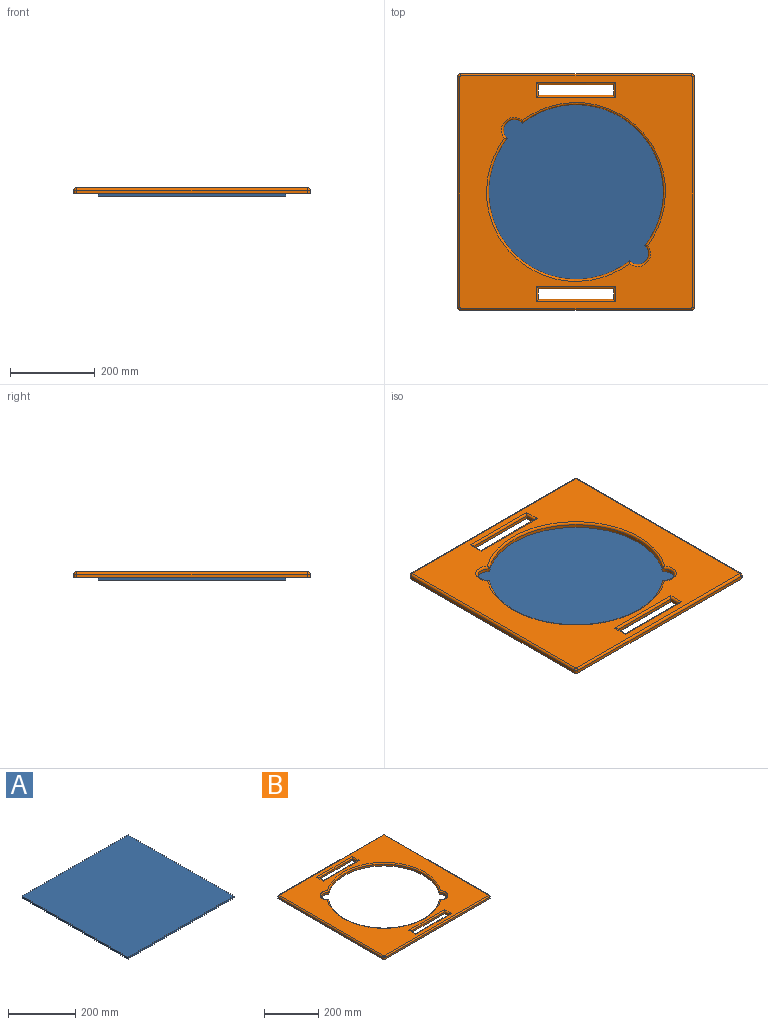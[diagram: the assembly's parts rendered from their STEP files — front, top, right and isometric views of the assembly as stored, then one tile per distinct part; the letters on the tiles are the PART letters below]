
ASSEMBLY  parts=2 mates=1
PART A: 6 faces, bbox 444.5x444.5x6.4 mm
  f0: plane 444.5x6.35mm, normal (0,-1,0), area 2822.6mm2, adj f1,f3,f4,f5
  f1: plane 444.5x6.35mm, normal (1,0,0), area 2822.6mm2, adj f0,f2,f4,f5
  f2: plane 444.5x6.35mm, normal (0,1,0), area 2822.6mm2, adj f1,f3,f4,f5
  f3: plane 444.5x6.35mm, normal (-1,0,0), area 2822.6mm2, adj f0,f2,f4,f5
  f4: plane 444.5x444.5mm, normal (0,0,1), area 197580.2mm2, adj f0,f1,f2,f3
  f5: plane 444.5x444.5mm, normal (0,0,-1), area 197580.2mm2, adj f0,f1,f2,f3
PART B: 42 faces, bbox 558.8x558.8x12.7 mm
  f0: plane 177.8x7.62mm, normal (0,-1,0), area 1354.8mm2, adj f1,f19,f21,f22
  f1: plane 25.4x7.62mm, normal (-1,0,0), area 193.5mm2, adj f0,f2,f21,f23
  f2: plane 177.8x7.62mm, normal (0,1,0), area 1354.8mm2, adj f1,f19,f21,f25
  f3: plane 546.1x7.62mm, normal (1,0,0), area 4161.3mm2, adj f4,f16,f21,f32
  f4: cylinder r=6.35mm len=7.62mm, axis (0,0,-1), area 76mm2, adj f3,f5,f21,f30
  f5: plane 546.1x7.62mm, normal (0,1,0), area 4161.3mm2, adj f4,f6,f21,f28
  f6: cylinder r=6.35mm len=7.62mm, axis (0,0,-1), area 76mm2, adj f5,f7,f21,f26
  f7: plane 546.1x7.62mm, normal (-1,0,0), area 4161.3mm2, adj f6,f8,f21,f27
  f8: cylinder r=6.35mm len=7.62mm, axis (0,0,-1), area 76mm2, adj f7,f9,f21,f29
  f9: plane 546.1x7.62mm, normal (0,-1,0), area 4161.3mm2, adj f8,f16,f21,f31
  f10: cylinder r=206.38mm len=333.27mm, axis (0,0,-1), area 4553.1mm2, adj f11,f17,f21,f35
  f11: cylinder r=25.4mm len=44.43mm, axis (0,0,-1), area 631.9mm2, adj f10,f12,f21,f34
  f12: cylinder r=206.38mm len=333.27mm, axis (0,0,-1), area 4553.1mm2, adj f11,f17,f21,f36
  f13: plane 25.4x7.62mm, normal (-1,0,0), area 193.5mm2, adj f14,f18,f21,f39
  f14: plane 177.8x7.62mm, normal (0,1,0), area 1354.8mm2, adj f13,f15,f21,f38
  f15: plane 25.4x7.62mm, normal (1,0,0), area 193.5mm2, adj f14,f18,f21,f40
  f16: cylinder r=6.35mm len=7.62mm, axis (0,0,-1), area 76mm2, adj f3,f9,f21,f33
  f17: cylinder r=25.4mm len=44.43mm, axis (0,0,-1), area 631.9mm2, adj f10,f12,f21,f37
  f18: plane 177.8x7.62mm, normal (0,-1,0), area 1354.8mm2, adj f13,f15,f21,f41
  f19: plane 25.4x7.62mm, normal (1,0,0), area 193.5mm2, adj f0,f2,f21,f24
  f20: plane 548.64x548.64mm, normal (0,0,1), area 144776.7mm2, adj f22,f23,f24,f25,f26,f27,f28,f29
  f21: plane 558.8x558.8mm, normal (0,0,-1), area 167308.4mm2, adj f0,f1,f2,f3,f4,f5,f6,f7
  f22: cylinder r=5.08mm len=187.96mm, axis (-1,0,0), area 1448.2mm2, adj f0,f20,f23,f24
  f23: cylinder r=5.08mm len=35.56mm, axis (0,1,0), area 232.1mm2, adj f1,f20,f22,f25
  f24: cylinder r=5.08mm len=35.56mm, axis (0,-1,0), area 232.1mm2, adj f19,f20,f22,f25
  f25: cylinder r=5.08mm len=187.96mm, axis (1,0,0), area 1448.2mm2, adj f2,f20,f23,f24
  f26: torus R=1.27mm, axis (0,0,1), area 56.5mm2, adj f6,f20,f27,f28
  f27: cylinder r=5.08mm len=546.1mm, axis (0,1,0), area 4357.7mm2, adj f7,f20,f26,f29
  f28: cylinder r=5.08mm len=546.1mm, axis (1,0,0), area 4357.7mm2, adj f5,f20,f26,f30
  f29: torus R=1.27mm, axis (0,0,1), area 56.5mm2, adj f8,f20,f27,f31
  f30: torus R=1.27mm, axis (0,0,1), area 56.5mm2, adj f4,f20,f28,f32
  f31: cylinder r=5.08mm len=546.1mm, axis (-1,0,0), area 4357.7mm2, adj f9,f20,f29,f33
  f32: cylinder r=5.08mm len=546.1mm, axis (0,-1,0), area 4357.7mm2, adj f3,f20,f30,f33
  f33: torus R=1.27mm, axis (0,0,1), area 56.5mm2, adj f16,f20,f31,f32
  f34: torus R=30.48mm, axis (0,0,1), area 682.1mm2, adj f11,f20,f35,f36
  f35: torus R=211.46mm, axis (0,0,1), area 4784.3mm2, adj f10,f20,f34,f37
  f36: torus R=211.46mm, axis (0,0,1), area 4784.3mm2, adj f12,f20,f34,f37
  f37: torus R=30.48mm, axis (0,0,1), area 682.1mm2, adj f17,f20,f35,f36
  f38: cylinder r=5.08mm len=187.96mm, axis (1,0,0), area 1448.2mm2, adj f14,f20,f39,f40
  f39: cylinder r=5.08mm len=35.56mm, axis (0,1,0), area 232.1mm2, adj f13,f20,f38,f41
  f40: cylinder r=5.08mm len=35.56mm, axis (0,-1,0), area 232.1mm2, adj f15,f20,f38,f41
  f41: cylinder r=5.08mm len=187.96mm, axis (-1,0,0), area 1448.2mm2, adj f18,f20,f39,f40
PLACE A t=(-965.05,440.29,-9.27)mm
PLACE B t=(-378.39,401.29,-2.92)mm
MATE fastened A.f4 <-> B.f10  axis (0,0,1) through (-1.46,1.59,-2.92)mm
